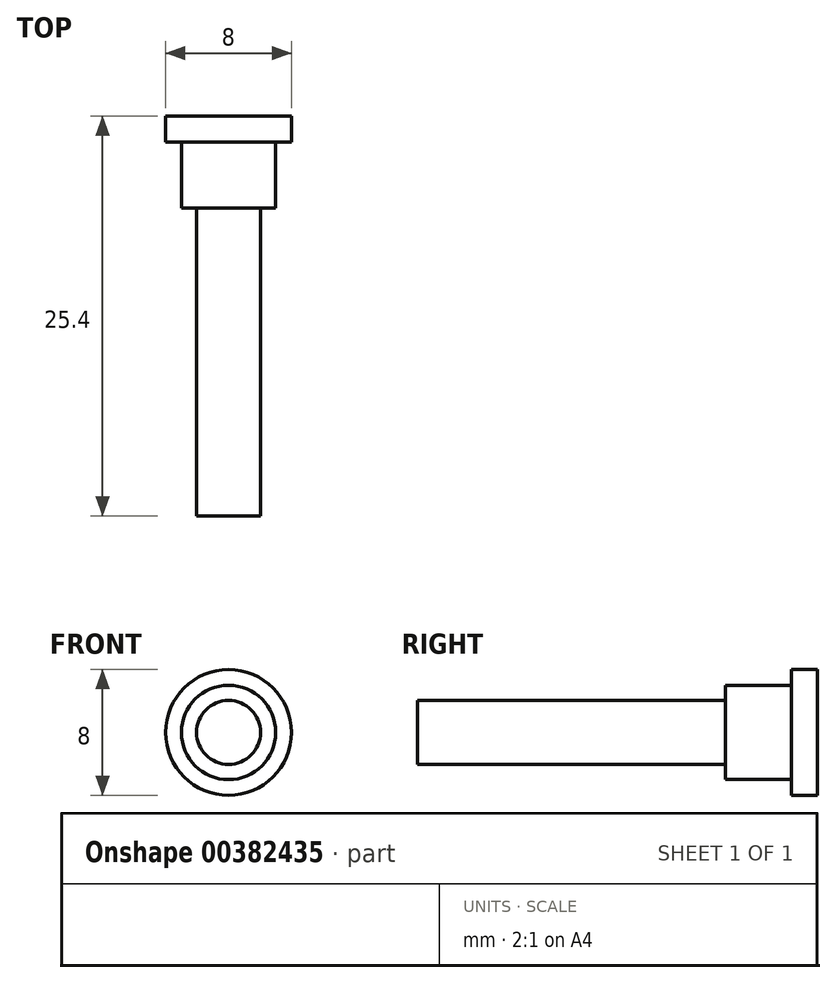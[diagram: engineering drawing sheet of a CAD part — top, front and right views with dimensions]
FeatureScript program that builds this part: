
annotation { "Feature Type Name" : "Feature", "Feature Type Description" : "" }
export const myFeature = defineFeature(function(context is Context, id is Id, definition is map)
    precondition{}
    {
        {
            var Q0;
            Q0=qCreatedBy(makeId("Front.planeOp"),FACE);
            var sketch = newSketch(context, id + "F0", { "sketchPlane" : qUnion([Q0])});
            skCircle(sketch, "E0", {"center": v(0, 0) * mm, "radius": 4 * mm});
            skCircle(sketch, "E1", {"center": v(0, 0) * mm, "radius": 3 * mm});
            skSolve(sketch);
        }
        {
            var Q0;
            Q0=makeQuery(id+"F0.imprint","IMPRINT",FACE,{"disambiguationData":[TD([[makeQuery(id+"F0.imprint","IMPRINT",EDGE,{"derivedFrom":sQuery(id+"F0.wireOp",EDGE,"E1")}),1.0]])]});
            extrude(context, id + "F1", {"entities" : qUnion([Q0]), "depth" : 5.84 * mm});
        }
        {
            var Q0;
            Q0 = qSketchRegion(id + "F0", true);
            extrude(context, id + "F2", {"entities" : qUnion([Q0]), "operationType" : NewBodyOperationType.ADD, "depth" : 1.65 * mm});
        }
        {
            var Q0;
            Q0=qCreatedBy(makeId("Front.planeOp"),FACE);
            var sketch = newSketch(context, id + "F3", { "sketchPlane" : qUnion([Q0])});
            skCircle(sketch, "E2", {"center": v(0, 0) * mm, "radius": 2.03 * mm});
            skSolve(sketch);
        }
        {
            var Q0;
            Q0 = qSketchRegion(id + "F3", true);
            extrude(context, id + "F4", {"entities" : qUnion([Q0]), "operationType" : NewBodyOperationType.ADD, "depth" : 25.4 * mm});
        }
    });
